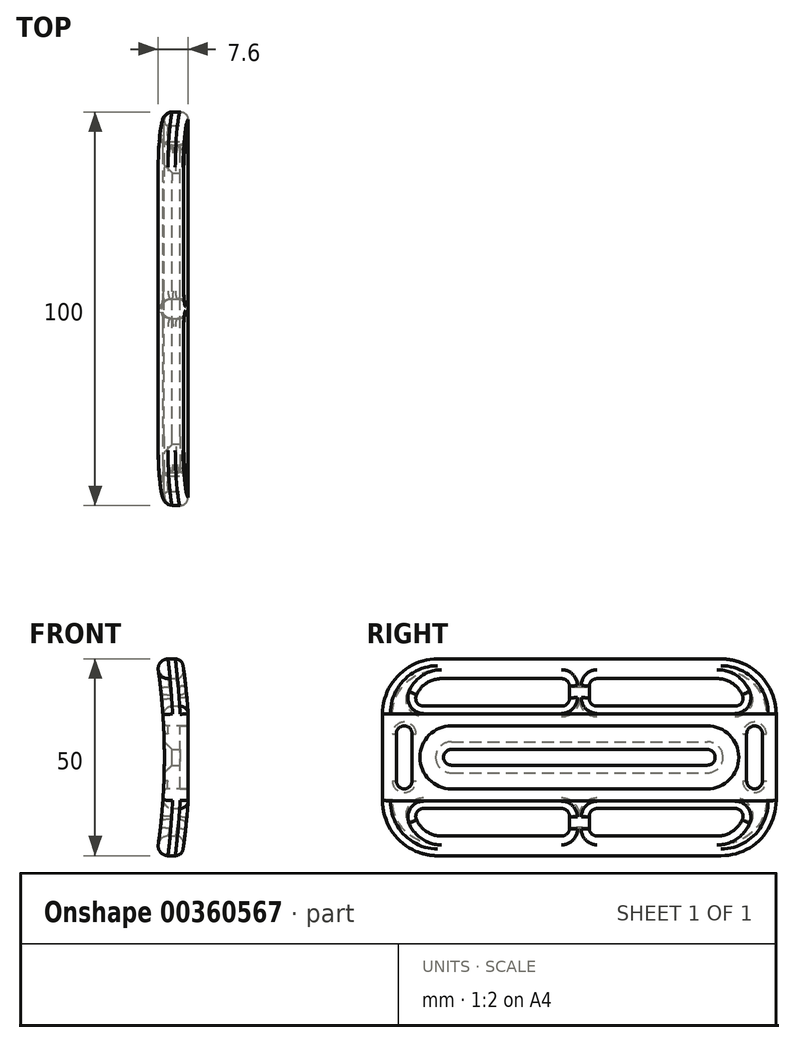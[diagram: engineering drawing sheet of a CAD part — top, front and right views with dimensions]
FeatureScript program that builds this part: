
annotation { "Feature Type Name" : "Feature", "Feature Type Description" : "" }
export const myFeature = defineFeature(function(context is Context, id is Id, definition is map)
    precondition{}
    {
        {
            var Q0;
            Q0=qCreatedBy(makeId("Front.planeOp"),FACE);
            var sketch = newSketch(context, id + "F0", { "sketchPlane" : qUnion([Q0])});
            skLineSegment(sketch, "E0.top", {"start": v(0, 25) * mm, "end": v(-8, 25) * mm});
            skLineSegment(sketch, "E0.left", {"start": v(0, 0) * mm, "end": v(0, 25) * mm});
            skLineSegment(sketch, "E0.right", {"start": v(-8, 0) * mm, "end": v(-8, 25) * mm});
            skLineSegment(sketch, "E1.top", {"start": v(0, -25) * mm, "end": v(-8, -25) * mm});
            skLineSegment(sketch, "E1.left", {"start": v(0, 0) * mm, "end": v(0, -25) * mm});
            skLineSegment(sketch, "E1.right", {"start": v(-8, 0) * mm, "end": v(-8, -25) * mm});
            skLineSegment(sketch, "E2.bottom", {"start": v(0, 8) * mm, "end": v(-2, 8) * mm});
            skLineSegment(sketch, "E2.top", {"start": v(0, -8) * mm, "end": v(-2, -8) * mm});
            skLineSegment(sketch, "E2.left", {"start": v(0, 8) * mm, "end": v(0, -8) * mm});
            skLineSegment(sketch, "E2.right", {"start": v(-2, 8) * mm, "end": v(-2, -8) * mm});
            skPoint(sketch, "E3.third.point", {"position": v(-196.82, -27.04) * mm});
            skArc(sketch, "E4", {"start": v(-8, -25) * mm, "mid": v(-6.03, 0) * mm, "end": v(-8, 25) * mm});
            skPoint(sketch, "E4.third.point", {"position": v(-14.66, -51.81) * mm});
            skArc(sketch, "E5.0", {"start": v(-1.52, -25) * mm, "mid": v(-0.61, -18.03) * mm, "end": v(0, -11.02) * mm});
            skArc(sketch, "E6.trimOffspring", {"start": v(0, 11.02) * mm, "mid": v(-0.61, 18.03) * mm, "end": v(-1.52, 25) * mm});
            skSolve(sketch);
        }
        {
            var Q0;
            Q0=makeQuery(id+"F0.imprint","IMPRINT",FACE,{"disambiguationData":[TD([[makeQuery(id+"F0.imprint","IMPRINT",EDGE,{"derivedFrom":sQuery(id+"F0.wireOp",EDGE,"E2.bottom")}),-1.0]])]});
            extrude(context, id + "F1", {"entities" : qUnion([Q0]), "depth" : 50 * mm, "hasSecondDirection" : true, "secondDirectionOppositeDirection" : true, "secondDirectionDepth" : 50 * mm});
        }
        {
            var Q0;
            Q0=makeQuery(id+"F1.opExtrude","CAP_EDGE",EDGE,{"disambiguationData":[OSD([sQuery(id+"F0.wireOp",EDGE,"E0.top")])],"isStart":false});
            var Q1;
            Q1=makeQuery(id+"F1.opExtrude","CAP_EDGE",EDGE,{"disambiguationData":[OSD([sQuery(id+"F0.wireOp",EDGE,"E0.top")])],"isStart":true});
            var Q2;
            Q2=makeQuery(id+"F1.opExtrude","CAP_EDGE",EDGE,{"disambiguationData":[OSD([sQuery(id+"F0.wireOp",EDGE,"E1.top")])],"isStart":false});
            var Q3;
            Q3=makeQuery(id+"F1.opExtrude","CAP_EDGE",EDGE,{"disambiguationData":[OSD([sQuery(id+"F0.wireOp",EDGE,"E1.top")])],"isStart":true});
            fillet(context, id + "F2", {"entities" : qUnion([Q0, Q1, Q2, Q3]), "radius" : 14 * mm, "tangentPropagation" : true, "allowEdgeOverflow" : false});
        }
        {
            var Q0;
            Q0=qCreatedBy(makeId("Right.planeOp"),FACE);
            var sketch = newSketch(context, id + "F3", { "sketchPlane" : qUnion([Q0])});
            skLineSegment(sketch, "E7.bottom", {"start": v(-35, 20) * mm, "end": v(-2.5, 20) * mm});
            skLineSegment(sketch, "E7.top", {"start": v(-35, 13) * mm, "end": v(-2.5, 13) * mm});
            skLineSegment(sketch, "E7.right", {"start": v(-2.5, 20) * mm, "end": v(-2.5, 13) * mm});
            skLineSegment(sketch, "E8.bottom", {"start": v(-2.5, -20) * mm, "end": v(-35, -20) * mm});
            skLineSegment(sketch, "E8.top", {"start": v(-2.5, -13) * mm, "end": v(-35, -13) * mm});
            skLineSegment(sketch, "E8.left", {"start": v(-2.5, -20) * mm, "end": v(-2.5, -13) * mm});
            skLineSegment(sketch, "E9", {"start": v(0, 0) * mm, "end": v(0, 52.93) * mm, "construction": true});
            skLineSegment(sketch, "E10", {"start": v(0, 52.93) * mm, "end": v(-1.44, 52.93) * mm, "construction": true});
            skLineSegment(sketch, "E11.MirrorCS", {"start": v(35, 20) * mm, "end": v(2.5, 20) * mm});
            skLineSegment(sketch, "E12.MirrorCS", {"start": v(2.5, 20) * mm, "end": v(2.5, 13) * mm});
            skLineSegment(sketch, "E13.MirrorCS", {"start": v(35, 13) * mm, "end": v(2.5, 13) * mm});
            skLineSegment(sketch, "E14.MirrorCS", {"start": v(2.5, -20) * mm, "end": v(35, -20) * mm});
            skLineSegment(sketch, "E15.MirrorCS", {"start": v(2.5, -13) * mm, "end": v(35, -13) * mm});
            skLineSegment(sketch, "E16.MirrorCS", {"start": v(2.5, -20) * mm, "end": v(2.5, -13) * mm});
            skLineSegment(sketch, "E17", {"start": v(-35, 13) * mm, "end": v(-42, 13) * mm});
            skLineSegment(sketch, "E18", {"start": v(42, 13) * mm, "end": v(35, 13) * mm});
            skLineSegment(sketch, "E19", {"start": v(35, -13) * mm, "end": v(42, -13) * mm});
            skLineSegment(sketch, "E20", {"start": v(-35, -13) * mm, "end": v(-42, -13) * mm});
            skArc(sketch, "E21", {"start": v(42, 13) * mm, "mid": v(39.95, 17.95) * mm, "end": v(35, 20) * mm});
            skArc(sketch, "E22", {"start": v(-35, 20) * mm, "mid": v(-39.95, 17.95) * mm, "end": v(-42, 13) * mm});
            skArc(sketch, "E23", {"start": v(-42, -13) * mm, "mid": v(-39.95, -17.95) * mm, "end": v(-35, -20) * mm});
            skArc(sketch, "E24", {"start": v(35, -20) * mm, "mid": v(39.95, -17.95) * mm, "end": v(42, -13) * mm});
            skPoint(sketch, "E25.MirrorCS.start.orphan", {"position": v(35, 20) * mm});
            skSolve(sketch);
        }
        {
            var Q0;
            Q0=makeQuery(id+"F3.imprint","IMPRINT",FACE,{"disambiguationData":[TD([[makeQuery(id+"F3.imprint","IMPRINT",EDGE,{"derivedFrom":sQuery(id+"F3.wireOp",EDGE,"E7.bottom")}),-1.0]])]});
            var Q1;
            Q1=makeQuery(id+"F3.imprint","IMPRINT",FACE,{"disambiguationData":[TD([[makeQuery(id+"F3.imprint","IMPRINT",EDGE,{"derivedFrom":sQuery(id+"F3.wireOp",EDGE,"aYIwaKne-w7pD-jzg0-wIrR-frMYWOzJamIR.bottom")}),1.0]])]});
            var Q2;
            Q2=makeQuery(id+"F3.imprint","IMPRINT",FACE,{"disambiguationData":[TD([[makeQuery(id+"F3.imprint","IMPRINT",EDGE,{"derivedFrom":sQuery(id+"F3.wireOp",EDGE,"dbu9yMfO-LKLj-5adb-XFTp-mxRKxUa9Af3I.bottom")}),1.0]])]});
            var Q3;
            Q3=makeQuery(id+"F3.imprint","IMPRINT",FACE,{"disambiguationData":[TD([[makeQuery(id+"F3.imprint","IMPRINT",EDGE,{"derivedFrom":sQuery(id+"F3.wireOp",EDGE,"E8.bottom")}),-1.0]])]});
            var Q4;
            Q4=makeQuery(id+"F3.imprint","IMPRINT",FACE,{"disambiguationData":[TD([[makeQuery(id+"F3.imprint","IMPRINT",EDGE,{"derivedFrom":sQuery(id+"F3.wireOp",EDGE,"E11.MirrorCS")}),1.0]])]});
            var Q5;
            Q5=makeQuery(id+"F3.imprint","IMPRINT",FACE,{"disambiguationData":[TD([[makeQuery(id+"F3.imprint","IMPRINT",EDGE,{"derivedFrom":sQuery(id+"F3.wireOp",EDGE,"a9c6f0e5-25e9-4c5a-a24e-b3d4f0bb53d11.MirrorCS")}),-1.0]])]});
            var Q6;
            Q6=makeQuery(id+"F3.imprint","IMPRINT",FACE,{"disambiguationData":[TD([[makeQuery(id+"F3.imprint","IMPRINT",EDGE,{"derivedFrom":sQuery(id+"F3.wireOp",EDGE,"a9c6f0e5-25e9-4c5a-a24e-b3d4f0bb53d10.MirrorCS")}),-1.0]])]});
            var Q7;
            Q7=makeQuery(id+"F3.imprint","IMPRINT",FACE,{"disambiguationData":[TD([[makeQuery(id+"F3.imprint","IMPRINT",EDGE,{"derivedFrom":sQuery(id+"F3.wireOp",EDGE,"E14.MirrorCS")}),1.0]])]});
            var Q8;
            Q8=makeQuery(id+"F3.imprint","IMPRINT",FACE,{"disambiguationData":[TD([[makeQuery(id+"F3.imprint","IMPRINT",EDGE,{"derivedFrom":sQuery(id+"F3.wireOp",EDGE,"E7.left")}),-1.0]])]});
            var Q9;
            Q9=makeQuery(id+"F3.imprint","IMPRINT",FACE,{"disambiguationData":[TD([[makeQuery(id+"F3.imprint","IMPRINT",EDGE,{"derivedFrom":sQuery(id+"F3.wireOp",EDGE,"E25.MirrorCS")}),1.0]])]});
            var Q10;
            Q10=makeQuery(id+"F3.imprint","IMPRINT",FACE,{"disambiguationData":[TD([[makeQuery(id+"F3.imprint","IMPRINT",EDGE,{"derivedFrom":sQuery(id+"F3.wireOp",EDGE,"6a068f12-1f97-4c15-ac1c-3f1accc7e67e0.MirrorCS")}),-1.0]])]});
            var Q11;
            Q11=makeQuery(id+"F3.imprint","IMPRINT",FACE,{"disambiguationData":[TD([[makeQuery(id+"F3.imprint","IMPRINT",EDGE,{"derivedFrom":sQuery(id+"F3.wireOp",EDGE,"E8.right")}),1.0]])]});
            extrude(context, id + "F4", {"entities" : qUnion([Q0, Q1, Q2, Q3, Q4, Q5, Q6, Q7, Q8, Q9, Q10, Q11]), "operationType" : NewBodyOperationType.REMOVE, "oppositeDirection" : true, "depth" : 25 * mm});
        }
        {
            var Q0;
            Q0=qCreatedBy(makeId("Right.planeOp"),FACE);
            var sketch = newSketch(context, id + "F5", { "sketchPlane" : qUnion([Q0])});
            skLineSegment(sketch, "E26.bottom", {"start": v(-34.5, 2) * mm, "end": v(34.5, 2) * mm});
            skLineSegment(sketch, "E26.top", {"start": v(-34.5, -2) * mm, "end": v(34.5, -2) * mm});
            skLineSegment(sketch, "E26.left", {"start": v(-34.5, 2) * mm, "end": v(-34.5, -2) * mm});
            skLineSegment(sketch, "E26.right", {"start": v(34.5, 2) * mm, "end": v(34.5, -2) * mm});
            skSolve(sketch);
        }
        {
            var Q0;
            Q0=makeQuery(id+"F5.imprint","IMPRINT",FACE,{"disambiguationData":[TD([[makeQuery(id+"F5.imprint","IMPRINT",EDGE,{"derivedFrom":sQuery(id+"F5.wireOp",EDGE,"E26.bottom")}),-1.0]])]});
            extrude(context, id + "F6", {"entities" : qUnion([Q0]), "operationType" : NewBodyOperationType.REMOVE, "oppositeDirection" : true, "depth" : 25 * mm});
        }
        {
            var Q0;
            Q0=qCreatedBy(makeId("Right.planeOp"),FACE);
            var sketch = newSketch(context, id + "F7", { "sketchPlane" : qUnion([Q0])});
            skLineSegment(sketch, "E27", {"start": v(0, 0) * mm, "end": v(-32.5, 0) * mm, "construction": true});
            skArc(sketch, "E28", {"start": v(-32.5, 8) * mm, "mid": v(-40.5, 0) * mm, "end": v(-32.5, -8) * mm});
            skLineSegment(sketch, "E29", {"start": v(0, 0) * mm, "end": v(32.5, 0) * mm, "construction": true});
            skArc(sketch, "E30", {"start": v(32.5, -8) * mm, "mid": v(40.5, 0) * mm, "end": v(32.5, 8) * mm});
            skLineSegment(sketch, "E31", {"start": v(-32.5, 0) * mm, "end": v(-32.5, -8) * mm, "construction": true});
            skLineSegment(sketch, "E32", {"start": v(-32.5, -8) * mm, "end": v(-50, -8) * mm});
            skLineSegment(sketch, "E33", {"start": v(-32.5, 0) * mm, "end": v(-32.5, 8) * mm, "construction": true});
            skLineSegment(sketch, "E34", {"start": v(-32.5, 8) * mm, "end": v(-50, 8) * mm});
            skLineSegment(sketch, "E35", {"start": v(-50, 8) * mm, "end": v(-50, -8) * mm});
            skLineSegment(sketch, "E36", {"start": v(32.5, 0) * mm, "end": v(32.5, 8) * mm, "construction": true});
            skLineSegment(sketch, "E37", {"start": v(32.5, 8) * mm, "end": v(50, 8) * mm});
            skLineSegment(sketch, "E38", {"start": v(32.5, 0) * mm, "end": v(32.5, -8) * mm, "construction": true});
            skLineSegment(sketch, "E39", {"start": v(32.5, -8) * mm, "end": v(50, -8) * mm});
            skLineSegment(sketch, "E40", {"start": v(50, -8) * mm, "end": v(50, 8) * mm});
            skPoint(sketch, "E41.orphan", {"position": v(51.81, 8) * mm});
            skSolve(sketch);
        }
        {
            var Q0;
            Q0=qSketchRegion(id+"F7",true);
            extrude(context, id + "F8", {"entities" : qUnion([Q0]), "operationType" : NewBodyOperationType.ADD, "oppositeDirection" : true, "depth" : 3 * mm});
        }
        {
            var Q0;
            Q0=makeQuery(id+"F4.boolean.opBoolean","COPY",EDGE,{"derivedFrom":makeQuery(id+"F4.opExtrude","SWEPT_EDGE",EDGE,{"disambiguationData":[OSD([sQuery(id+"F3.wireOp",EDGE,"E7.bottom"),sQuery(id+"F3.wireOp",EDGE,"E7.right")])]})});
            var Q1;
            Q1=makeQuery(id+"F4.boolean.opBoolean","COPY",EDGE,{"derivedFrom":makeQuery(id+"F4.opExtrude","SWEPT_EDGE",EDGE,{"disambiguationData":[OSD([sQuery(id+"F3.wireOp",EDGE,"E8.top"),sQuery(id+"F3.wireOp",EDGE,"E8.left")])]})});
            var Q2;
            Q2=makeQuery(id+"F4.boolean.opBoolean","COPY",EDGE,{"derivedFrom":makeQuery(id+"F4.opExtrude","SWEPT_EDGE",EDGE,{"disambiguationData":[OSD([sQuery(id+"F3.wireOp",EDGE,"E8.bottom"),sQuery(id+"F3.wireOp",EDGE,"E8.left")])]})});
            var Q3;
            Q3=makeQuery(id+"F4.boolean.opBoolean","COPY",EDGE,{"derivedFrom":makeQuery(id+"F4.opExtrude","SWEPT_EDGE",EDGE,{"disambiguationData":[OSD([sQuery(id+"F3.wireOp",EDGE,"E7.top"),sQuery(id+"F3.wireOp",EDGE,"E7.right")])]})});
            var Q4;
            Q4=makeQuery(id+"F4.boolean.opBoolean","COPY",EDGE,{"derivedFrom":makeQuery(id+"F4.opExtrude","SWEPT_EDGE",EDGE,{"disambiguationData":[OSD([sQuery(id+"F3.wireOp",EDGE,"E18"),sQuery(id+"F3.wireOp",EDGE,"E21")])]})});
            var Q5;
            Q5=makeQuery(id+"F4.boolean.opBoolean","COPY",EDGE,{"derivedFrom":makeQuery(id+"F4.opExtrude","SWEPT_EDGE",EDGE,{"disambiguationData":[OSD([sQuery(id+"F3.wireOp",EDGE,"E19"),sQuery(id+"F3.wireOp",EDGE,"E24")])]})});
            var Q6;
            Q6=makeQuery(id+"F4.boolean.opBoolean","COPY",EDGE,{"derivedFrom":makeQuery(id+"F4.opExtrude","SWEPT_EDGE",EDGE,{"disambiguationData":[OSD([sQuery(id+"F3.wireOp",EDGE,"E11.MirrorCS"),sQuery(id+"F3.wireOp",EDGE,"E12.MirrorCS")])]})});
            var Q7;
            Q7=makeQuery(id+"F4.boolean.opBoolean","COPY",EDGE,{"derivedFrom":makeQuery(id+"F4.opExtrude","SWEPT_EDGE",EDGE,{"disambiguationData":[OSD([sQuery(id+"F3.wireOp",EDGE,"E15.MirrorCS"),sQuery(id+"F3.wireOp",EDGE,"E16.MirrorCS")])]})});
            var Q8;
            Q8=makeQuery(id+"F4.boolean.opBoolean","COPY",EDGE,{"derivedFrom":makeQuery(id+"F4.opExtrude","SWEPT_EDGE",EDGE,{"disambiguationData":[OSD([sQuery(id+"F3.wireOp",EDGE,"E20"),sQuery(id+"F3.wireOp",EDGE,"E23")])]})});
            var Q9;
            Q9=makeQuery(id+"F4.boolean.opBoolean","COPY",EDGE,{"derivedFrom":makeQuery(id+"F4.opExtrude","SWEPT_EDGE",EDGE,{"disambiguationData":[OSD([sQuery(id+"F3.wireOp",EDGE,"E12.MirrorCS"),sQuery(id+"F3.wireOp",EDGE,"E13.MirrorCS")])]})});
            var Q10;
            Q10=makeQuery(id+"F4.boolean.opBoolean","COPY",EDGE,{"derivedFrom":makeQuery(id+"F4.opExtrude","SWEPT_EDGE",EDGE,{"disambiguationData":[OSD([sQuery(id+"F3.wireOp",EDGE,"E14.MirrorCS"),sQuery(id+"F3.wireOp",EDGE,"E16.MirrorCS")])]})});
            var Q11;
            Q11=makeQuery(id+"F4.boolean.opBoolean","COPY",EDGE,{"derivedFrom":makeQuery(id+"F4.opExtrude","SWEPT_EDGE",EDGE,{"disambiguationData":[OSD([sQuery(id+"F3.wireOp",EDGE,"E17"),sQuery(id+"F3.wireOp",EDGE,"E22")])]})});
            fillet(context, id + "F9", {"entities" : qUnion([Q0, Q1, Q2, Q3, Q4, Q5, Q6, Q7, Q8, Q9, Q10, Q11]), "radius" : 2 * mm, "tangentPropagation" : true, "allowEdgeOverflow" : false});
        }
        {
            var Q0;
            Q0=makeQuery(id+"F6.boolean.opBoolean","COPY",EDGE,{"derivedFrom":makeQuery(id+"F6.opExtrude","SWEPT_EDGE",EDGE,{"disambiguationData":[OSD([sQuery(id+"F5.wireOp",EDGE,"E26.top"),sQuery(id+"F5.wireOp",EDGE,"E26.right")])]})});
            var Q1;
            Q1=makeQuery(id+"F6.boolean.opBoolean","COPY",EDGE,{"derivedFrom":makeQuery(id+"F6.opExtrude","SWEPT_EDGE",EDGE,{"disambiguationData":[OSD([sQuery(id+"F5.wireOp",EDGE,"E26.top"),sQuery(id+"F5.wireOp",EDGE,"E26.left")])]})});
            var Q2;
            Q2=makeQuery(id+"F6.boolean.opBoolean","COPY",EDGE,{"derivedFrom":makeQuery(id+"F6.opExtrude","SWEPT_EDGE",EDGE,{"disambiguationData":[OSD([sQuery(id+"F5.wireOp",EDGE,"E26.bottom"),sQuery(id+"F5.wireOp",EDGE,"E26.right")])]})});
            var Q3;
            Q3=makeQuery(id+"F6.boolean.opBoolean","COPY",EDGE,{"derivedFrom":makeQuery(id+"F6.opExtrude","SWEPT_EDGE",EDGE,{"disambiguationData":[OSD([sQuery(id+"F5.wireOp",EDGE,"E26.bottom"),sQuery(id+"F5.wireOp",EDGE,"E26.left")])]})});
            fillet(context, id + "F10", {"entities" : qUnion([Q0, Q1, Q2, Q3]), "radius" : 2 * mm, "tangentPropagation" : true, "allowEdgeOverflow" : false});
        }
        {
            var Q0;
            Q0=makeQuery(id+"F6.boolean.opBoolean","INTERSECT",EDGE,{"derivedFrom":[makeQuery(id+"F1.opExtrude","SWEPT_FACE",FACE,{"disambiguationData":[OSD([sQuery(id+"F0.wireOp",EDGE,"E4")])]}),makeQuery(id+"F6.opExtrude","SWEPT_FACE",FACE,{"disambiguationData":[OSD([sQuery(id+"F5.wireOp",EDGE,"E26.bottom")])]})]});
            chamfer(context, id + "F11", {"entities" : qUnion([Q0]), "width" : 2 * mm, "tangentPropagation" : true});
        }
        {
            var Q0;
            Q0=makeQuery(id+"F4.boolean.opBoolean","INTERSECT",EDGE,{"derivedFrom":[makeQuery(id+"F1.opExtrude","SWEPT_FACE",FACE,{"disambiguationData":[OSD([sQuery(id+"F0.wireOp",EDGE,"E4")])]}),makeQuery(id+"F4.opExtrude","SWEPT_FACE",FACE,{"disambiguationData":[OSD([sQuery(id+"F3.wireOp",EDGE,"E11.MirrorCS")])]})]});
            var Q1;
            Q1=makeQuery(id+"F4.boolean.opBoolean","INTERSECT",EDGE,{"derivedFrom":[makeQuery(id+"F1.opExtrude","SWEPT_FACE",FACE,{"disambiguationData":[OSD([sQuery(id+"F0.wireOp",EDGE,"E4")])]}),makeQuery(id+"F4.opExtrude","SWEPT_FACE",FACE,{"disambiguationData":[OSD([sQuery(id+"F3.wireOp",EDGE,"E7.bottom")])]})]});
            var Q2;
            Q2=makeQuery(id+"F4.boolean.opBoolean","INTERSECT",EDGE,{"derivedFrom":[makeQuery(id+"F1.opExtrude","SWEPT_FACE",FACE,{"disambiguationData":[OSD([sQuery(id+"F0.wireOp",EDGE,"E4")])]}),makeQuery(id+"F4.opExtrude","SWEPT_FACE",FACE,{"disambiguationData":[OSD([sQuery(id+"F3.wireOp",EDGE,"E15.MirrorCS"),sQuery(id+"F3.wireOp",EDGE,"E19")])]})]});
            var Q3;
            Q3=makeQuery(id+"F4.boolean.opBoolean","INTERSECT",EDGE,{"derivedFrom":[makeQuery(id+"F1.opExtrude","SWEPT_FACE",FACE,{"disambiguationData":[OSD([sQuery(id+"F0.wireOp",EDGE,"E4")])]}),makeQuery(id+"F4.opExtrude","SWEPT_FACE",FACE,{"disambiguationData":[OSD([sQuery(id+"F3.wireOp",EDGE,"E8.top"),sQuery(id+"F3.wireOp",EDGE,"E20")])]})]});
            var Q4;
            Q4=makeQuery(id+"F1.opExtrude","SWEPT_EDGE",EDGE,{"disambiguationData":[OSD([sQuery(id+"F0.wireOp",EDGE,"E0.top"),sQuery(id+"F0.wireOp",EDGE,"E0.right"),sQuery(id+"F0.wireOp",EDGE,"E4")])]});
            fillet(context, id + "F12", {"entities" : qUnion([Q0, Q1, Q2, Q3, Q4]), "radius" : 2.5 * mm, "tangentPropagation" : true, "allowEdgeOverflow" : false});
        }
        {
            var Q0;
            Q0=makeQuery(id+"F4.boolean.opBoolean","INTERSECT",EDGE,{"derivedFrom":[makeQuery(id+"F1.opExtrude","SWEPT_FACE",FACE,{"disambiguationData":[OSD([sQuery(id+"F0.wireOp",EDGE,"E6.trimOffspring")])]}),makeQuery(id+"F4.opExtrude","SWEPT_FACE",FACE,{"disambiguationData":[OSD([sQuery(id+"F3.wireOp",EDGE,"E7.bottom")])]})]});
            var Q1;
            Q1=makeQuery(id+"F4.boolean.opBoolean","INTERSECT",EDGE,{"derivedFrom":[makeQuery(id+"F1.opExtrude","SWEPT_FACE",FACE,{"disambiguationData":[OSD([sQuery(id+"F0.wireOp",EDGE,"E6.trimOffspring")])]}),makeQuery(id+"F4.opExtrude","SWEPT_FACE",FACE,{"disambiguationData":[OSD([sQuery(id+"F3.wireOp",EDGE,"E11.MirrorCS")])]})]});
            var Q2;
            Q2=makeQuery(id+"F4.boolean.opBoolean","INTERSECT",EDGE,{"derivedFrom":[makeQuery(id+"F1.opExtrude","SWEPT_FACE",FACE,{"disambiguationData":[OSD([sQuery(id+"F0.wireOp",EDGE,"E5.0")])]}),makeQuery(id+"F4.opExtrude","SWEPT_FACE",FACE,{"disambiguationData":[OSD([sQuery(id+"F3.wireOp",EDGE,"E15.MirrorCS"),sQuery(id+"F3.wireOp",EDGE,"E19")])]})]});
            var Q3;
            Q3=makeQuery(id+"F4.boolean.opBoolean","INTERSECT",EDGE,{"derivedFrom":[makeQuery(id+"F1.opExtrude","SWEPT_FACE",FACE,{"disambiguationData":[OSD([sQuery(id+"F0.wireOp",EDGE,"E5.0")])]}),makeQuery(id+"F4.opExtrude","SWEPT_FACE",FACE,{"disambiguationData":[OSD([sQuery(id+"F3.wireOp",EDGE,"E8.top"),sQuery(id+"F3.wireOp",EDGE,"E20")])]})]});
            fillet(context, id + "F13", {"entities" : qUnion([Q0, Q1, Q2, Q3]), "radius" : 2 * mm, "tangentPropagation" : true, "allowEdgeOverflow" : false});
        }
        {
            var Q0;
            Q0=makeQuery(id+"F2.opFillet","BLEND_EDGE",EDGE,{"blendedFrom":[makeQuery(id+"F1.opExtrude","CAP_EDGE",EDGE,{"disambiguationData":[OSD([sQuery(id+"F0.wireOp",EDGE,"E0.top")])],"isStart":true}),makeQuery(id+"F1.opExtrude","SWEPT_FACE",FACE,{"disambiguationData":[OSD([sQuery(id+"F0.wireOp",EDGE,"E6.trimOffspring")])]})],"blendedInto":[makeQuery(id+"F1.opExtrude","SWEPT_FACE",FACE,{"disambiguationData":[OSD([sQuery(id+"F0.wireOp",EDGE,"E6.trimOffspring")])]})]});
            var Q1;
            Q1=makeQuery(id+"F2.opFillet","BLEND_EDGE",EDGE,{"blendedFrom":[makeQuery(id+"F1.opExtrude","CAP_EDGE",EDGE,{"disambiguationData":[OSD([sQuery(id+"F0.wireOp",EDGE,"E1.top")])],"isStart":true}),makeQuery(id+"F1.opExtrude","SWEPT_FACE",FACE,{"disambiguationData":[OSD([sQuery(id+"F0.wireOp",EDGE,"E5.0")])]})],"blendedInto":[makeQuery(id+"F1.opExtrude","SWEPT_FACE",FACE,{"disambiguationData":[OSD([sQuery(id+"F0.wireOp",EDGE,"E5.0")])]})]});
            fillet(context, id + "F14", {"entities" : qUnion([Q0, Q1]), "radius" : 2 * mm, "tangentPropagation" : true, "allowEdgeOverflow" : false});
        }
        {
            var Q0;
            Q0=qCreatedBy(makeId("Right.planeOp"),FACE);
            var sketch = newSketch(context, id + "F15", { "sketchPlane" : qUnion([Q0])});
            skLineSegment(sketch, "E42", {"start": v(0, 0) * mm, "end": v(-42.5, 0) * mm, "construction": true});
            skLineSegment(sketch, "E43", {"start": v(0, 0) * mm, "end": v(42.5, 0) * mm, "construction": true});
            skLineSegment(sketch, "E44.bottom", {"start": v(-42.5, 0) * mm, "end": v(-46.5, 0) * mm});
            skLineSegment(sketch, "E44.top", {"start": v(-42.5, 8) * mm, "end": v(-46.5, 8) * mm});
            skLineSegment(sketch, "E44.left", {"start": v(-42.5, 0) * mm, "end": v(-42.5, 8) * mm});
            skLineSegment(sketch, "E44.right", {"start": v(-46.5, 0) * mm, "end": v(-46.5, 8) * mm});
            skLineSegment(sketch, "E45.top", {"start": v(-42.5, -8) * mm, "end": v(-46.5, -8) * mm});
            skLineSegment(sketch, "E45.left", {"start": v(-42.5, 0) * mm, "end": v(-42.5, -8) * mm});
            skLineSegment(sketch, "E45.right", {"start": v(-46.5, 0) * mm, "end": v(-46.5, -8) * mm});
            skLineSegment(sketch, "E46.bottom", {"start": v(42.5, 8) * mm, "end": v(46.5, 8) * mm});
            skLineSegment(sketch, "E46.top", {"start": v(42.5, -8) * mm, "end": v(46.5, -8) * mm});
            skLineSegment(sketch, "E46.left", {"start": v(42.5, 8) * mm, "end": v(42.5, -8) * mm});
            skLineSegment(sketch, "E46.right", {"start": v(46.5, 8) * mm, "end": v(46.5, -8) * mm});
            skSolve(sketch);
        }
        {
            var Q0;
            Q0=makeQuery(id+"F15.imprint","IMPRINT",FACE,{"disambiguationData":[TD([[makeQuery(id+"F15.imprint","IMPRINT",EDGE,{"derivedFrom":sQuery(id+"F15.wireOp",EDGE,"E46.bottom")}),-1.0]])]});
            var Q1;
            Q1=makeQuery(id+"F15.imprint","IMPRINT",FACE,{"disambiguationData":[TD([[makeQuery(id+"F15.imprint","IMPRINT",EDGE,{"derivedFrom":sQuery(id+"F15.wireOp",EDGE,"E44.bottom")}),1.0]])]});
            var Q2;
            Q2=makeQuery(id+"F15.imprint","IMPRINT",FACE,{"disambiguationData":[TD([[makeQuery(id+"F15.imprint","IMPRINT",EDGE,{"derivedFrom":sQuery(id+"F15.wireOp",EDGE,"E44.top")}),1.0]])]});
            extrude(context, id + "F16", {"entities" : qUnion([Q0, Q1, Q2]), "operationType" : NewBodyOperationType.REMOVE, "oppositeDirection" : true, "depth" : 25 * mm});
        }
        {
            var Q0;
            Q0=makeQuery(id+"F16.boolean.opBoolean","COPY",EDGE,{"derivedFrom":makeQuery(id+"F16.opExtrude","SWEPT_EDGE",EDGE,{"disambiguationData":[OSD([sQuery(id+"F15.wireOp",EDGE,"E44.top"),sQuery(id+"F15.wireOp",EDGE,"E44.right")])]})});
            var Q1;
            Q1=makeQuery(id+"F16.boolean.opBoolean","COPY",EDGE,{"derivedFrom":makeQuery(id+"F16.opExtrude","SWEPT_EDGE",EDGE,{"disambiguationData":[OSD([sQuery(id+"F15.wireOp",EDGE,"E46.bottom"),sQuery(id+"F15.wireOp",EDGE,"E46.left")])]})});
            var Q2;
            Q2=makeQuery(id+"F16.boolean.opBoolean","COPY",EDGE,{"derivedFrom":makeQuery(id+"F16.opExtrude","SWEPT_EDGE",EDGE,{"disambiguationData":[OSD([sQuery(id+"F15.wireOp",EDGE,"E46.bottom"),sQuery(id+"F15.wireOp",EDGE,"E46.right")])]})});
            var Q3;
            Q3=makeQuery(id+"F16.boolean.opBoolean","COPY",EDGE,{"derivedFrom":makeQuery(id+"F16.opExtrude","SWEPT_EDGE",EDGE,{"disambiguationData":[OSD([sQuery(id+"F15.wireOp",EDGE,"E44.top"),sQuery(id+"F15.wireOp",EDGE,"E44.left")])]})});
            var Q4;
            Q4=makeQuery(id+"F16.boolean.opBoolean","COPY",EDGE,{"derivedFrom":makeQuery(id+"F16.opExtrude","SWEPT_EDGE",EDGE,{"disambiguationData":[OSD([sQuery(id+"F15.wireOp",EDGE,"E46.top"),sQuery(id+"F15.wireOp",EDGE,"E46.right")])]})});
            var Q5;
            Q5=makeQuery(id+"F16.boolean.opBoolean","COPY",EDGE,{"derivedFrom":makeQuery(id+"F16.opExtrude","SWEPT_EDGE",EDGE,{"disambiguationData":[OSD([sQuery(id+"F15.wireOp",EDGE,"E45.top"),sQuery(id+"F15.wireOp",EDGE,"E45.left")])]})});
            var Q6;
            Q6=makeQuery(id+"F16.boolean.opBoolean","COPY",EDGE,{"derivedFrom":makeQuery(id+"F16.opExtrude","SWEPT_EDGE",EDGE,{"disambiguationData":[OSD([sQuery(id+"F15.wireOp",EDGE,"E46.top"),sQuery(id+"F15.wireOp",EDGE,"E46.left")])]})});
            var Q7;
            Q7=makeQuery(id+"F16.boolean.opBoolean","COPY",EDGE,{"derivedFrom":makeQuery(id+"F16.opExtrude","SWEPT_EDGE",EDGE,{"disambiguationData":[OSD([sQuery(id+"F15.wireOp",EDGE,"E45.top"),sQuery(id+"F15.wireOp",EDGE,"E45.right")])]})});
            fillet(context, id + "F17", {"entities" : qUnion([Q0, Q1, Q2, Q3, Q4, Q5, Q6, Q7]), "radius" : 2 * mm, "tangentPropagation" : true, "allowEdgeOverflow" : false});
        }
        {
            var Q0;
            Q0=makeQuery(id+"F16.boolean.opBoolean","INTERSECT",EDGE,{"derivedFrom":[makeQuery(id+"F12.opFillet","SPLIT",FACE,{"disambiguationData":[OD(2.0)],"derivedFrom":makeQuery(id+"F1.opExtrude","SWEPT_FACE",FACE,{"disambiguationData":[OSD([sQuery(id+"F0.wireOp",EDGE,"E4")])]})}),makeQuery(id+"F16.opExtrude","SWEPT_FACE",FACE,{"disambiguationData":[OSD([sQuery(id+"F15.wireOp",EDGE,"E44.right"),sQuery(id+"F15.wireOp",EDGE,"E45.right")])]})]});
            var Q1;
            Q1=makeQuery(id+"F16.boolean.opBoolean","INTERSECT",EDGE,{"derivedFrom":[makeQuery(id+"F12.opFillet","SPLIT",FACE,{"disambiguationData":[OD(2.0)],"derivedFrom":makeQuery(id+"F1.opExtrude","SWEPT_FACE",FACE,{"disambiguationData":[OSD([sQuery(id+"F0.wireOp",EDGE,"E4")])]})}),makeQuery(id+"F16.opExtrude","SWEPT_FACE",FACE,{"disambiguationData":[OSD([sQuery(id+"F15.wireOp",EDGE,"E46.left")])]})]});
            var Q2;
            Q2=makeQuery(id+"F16.boolean.opBoolean","COPY",EDGE,{"derivedFrom":makeQuery(id+"F16.opExtrude","CAP_EDGE",EDGE,{"disambiguationData":[OSD([sQuery(id+"F15.wireOp",EDGE,"E46.right")])],"isStart":true})});
            var Q3;
            Q3=makeQuery(id+"F16.boolean.opBoolean","COPY",EDGE,{"derivedFrom":makeQuery(id+"F16.opExtrude","CAP_EDGE",EDGE,{"disambiguationData":[OSD([sQuery(id+"F15.wireOp",EDGE,"E44.left"),sQuery(id+"F15.wireOp",EDGE,"E45.left")])],"isStart":true})});
            fillet(context, id + "F18", {"entities" : qUnion([Q0, Q1, Q2, Q3]), "radius" : 1 * mm, "tangentPropagation" : true, "allowEdgeOverflow" : false});
        }
    });
